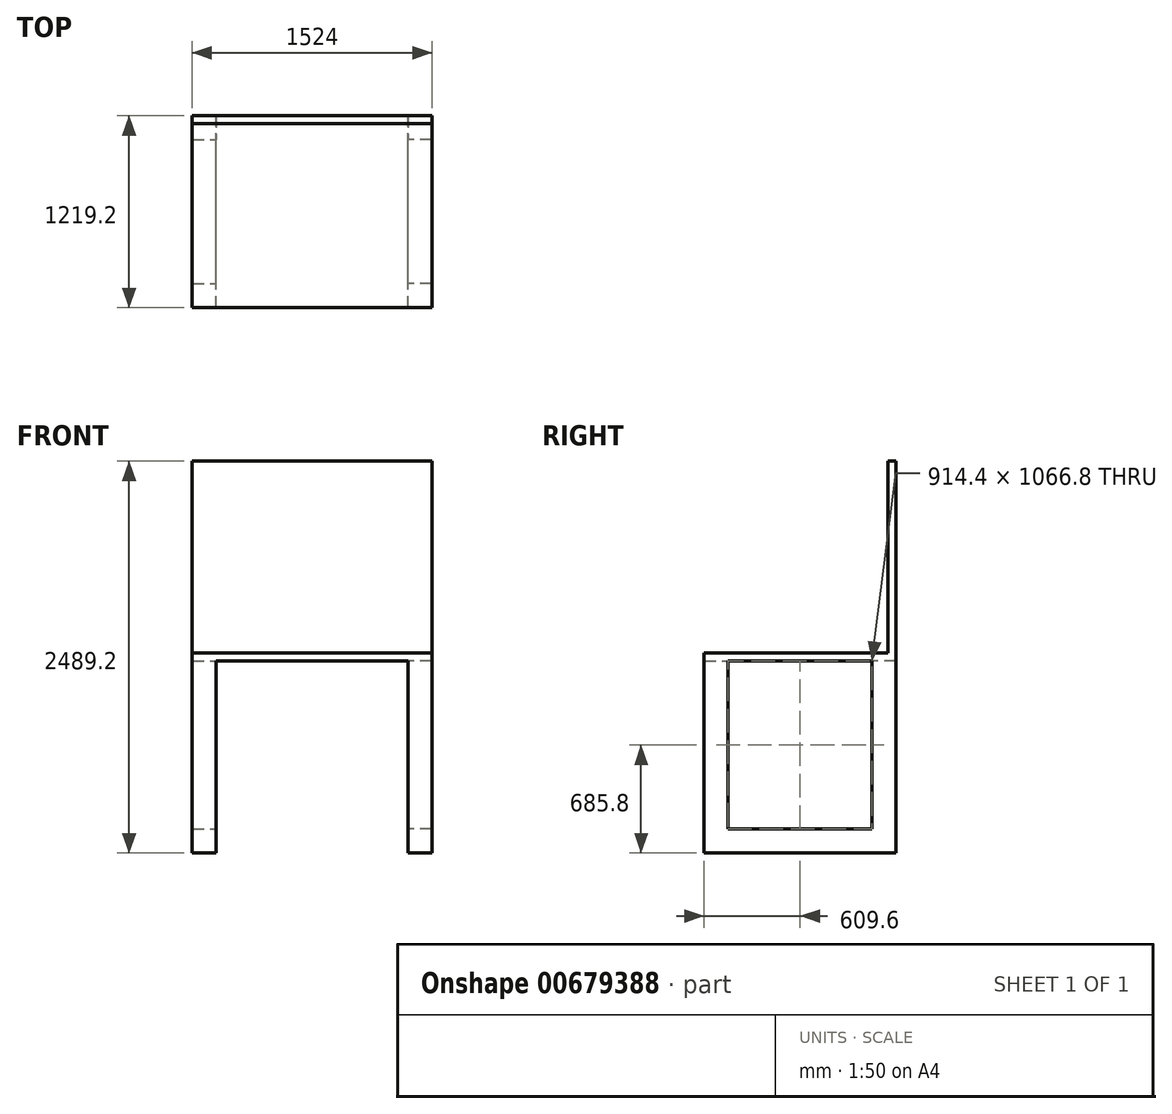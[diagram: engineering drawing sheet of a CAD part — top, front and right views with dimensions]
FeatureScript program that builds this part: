
annotation { "Feature Type Name" : "Feature", "Feature Type Description" : "" }
export const myFeature = defineFeature(function(context is Context, id is Id, definition is map)
    precondition{}
    {
        {
            var Q0;
            Q0=qCreatedBy(makeId("Front.planeOp"),FACE);
            var sketch = newSketch(context, id + "F0", { "sketchPlane" : qUnion([Q0])});
            skLineSegment(sketch, "E0.bottom", {"start": v(0, 0) * mm, "end": v(1524, 0) * mm});
            skLineSegment(sketch, "E0.top", {"start": v(0, 1219.2) * mm, "end": v(1524, 1219.2) * mm});
            skLineSegment(sketch, "E0.left", {"start": v(0, 0) * mm, "end": v(0, 1219.2) * mm});
            skLineSegment(sketch, "E0.right", {"start": v(1524, 0) * mm, "end": v(1524, 1219.2) * mm});
            skSolve(sketch);
        }
        {
            var Q0;
            Q0 = qSketchRegion(id + "F0", true);
            extrude(context, id + "F1", {"entities" : qUnion([Q0]), "depth" : 50.8 * mm, "offsetDistance" : 25.4 * mm});
        }
        {
            var Q0;
            Q0=makeQuery(id+"F1.opExtrude","SWEPT_FACE",FACE,{"disambiguationData":[OSD([sQuery(id+"F0.wireOp",EDGE,"E0.bottom")])]});
            var sketch = newSketch(context, id + "F2", { "sketchPlane" : qUnion([Q0])});
            skLineSegment(sketch, "E1.bottom", {"start": v(0, 0) * mm, "end": v(1524, 0) * mm});
            skLineSegment(sketch, "E1.top", {"start": v(0, 1219.2) * mm, "end": v(1524, 1219.2) * mm});
            skLineSegment(sketch, "E1.left", {"start": v(0, 0) * mm, "end": v(0, 1219.2) * mm});
            skLineSegment(sketch, "E1.right", {"start": v(1524, 0) * mm, "end": v(1524, 1219.2) * mm});
            skSolve(sketch);
        }
        {
            var Q0;
            Q0 = qSketchRegion(id + "F2", true);
            extrude(context, id + "F3", {"entities" : qUnion([Q0]), "operationType" : NewBodyOperationType.ADD, "depth" : 50.8 * mm, "offsetDistance" : 25.4 * mm});
        }
        {
            var Q0;
            Q0=makeQuery(id+"F3.opExtrude","CAP_FACE",FACE,{"disambiguationData":[OSD([sQuery(id+"F2.wireOp",EDGE,"E1.bottom"),sQuery(id+"F2.wireOp",EDGE,"E1.top"),sQuery(id+"F2.wireOp",EDGE,"E1.left"),sQuery(id+"F2.wireOp",EDGE,"E1.right")])],"isStart":false});
            var sketch = newSketch(context, id + "F4", { "sketchPlane" : qUnion([Q0])});
            skLineSegment(sketch, "E2.bottom", {"start": v(0, 1219.2) * mm, "end": v(152.4, 1219.2) * mm});
            skLineSegment(sketch, "E2.top", {"start": v(0, 1066.8) * mm, "end": v(152.4, 1066.8) * mm});
            skLineSegment(sketch, "E2.left", {"start": v(0, 1219.2) * mm, "end": v(0, 1066.8) * mm});
            skLineSegment(sketch, "E2.right", {"start": v(152.4, 1219.2) * mm, "end": v(152.4, 1066.8) * mm});
            skLineSegment(sketch, "E3.bottom", {"start": v(1524, 1219.2) * mm, "end": v(1371.6, 1219.2) * mm});
            skLineSegment(sketch, "E3.top", {"start": v(1524, 1066.8) * mm, "end": v(1371.6, 1066.8) * mm});
            skLineSegment(sketch, "E3.left", {"start": v(1524, 1219.2) * mm, "end": v(1524, 1066.8) * mm});
            skLineSegment(sketch, "E3.right", {"start": v(1371.6, 1219.2) * mm, "end": v(1371.6, 1066.8) * mm});
            skLineSegment(sketch, "E4.bottom", {"start": v(1524, 0) * mm, "end": v(1371.6, 0) * mm});
            skLineSegment(sketch, "E4.top", {"start": v(1524, 152.4) * mm, "end": v(1371.6, 152.4) * mm});
            skLineSegment(sketch, "E4.left", {"start": v(1524, 0) * mm, "end": v(1524, 152.4) * mm});
            skLineSegment(sketch, "E4.right", {"start": v(1371.6, 0) * mm, "end": v(1371.6, 152.4) * mm});
            skLineSegment(sketch, "E5.bottom", {"start": v(0, 0) * mm, "end": v(152.4, 0) * mm});
            skLineSegment(sketch, "E5.top", {"start": v(0, 152.4) * mm, "end": v(152.4, 152.4) * mm});
            skLineSegment(sketch, "E5.left", {"start": v(0, 0) * mm, "end": v(0, 152.4) * mm});
            skLineSegment(sketch, "E5.right", {"start": v(152.4, 0) * mm, "end": v(152.4, 152.4) * mm});
            skSolve(sketch);
        }
        {
            var Q0;
            Q0 = qSketchRegion(id + "F4", true);
            extrude(context, id + "F5", {"entities" : qUnion([Q0]), "operationType" : NewBodyOperationType.ADD, "depth" : 1219.2 * mm, "offsetDistance" : 25.4 * mm});
        }
        {
            var Q0;
            Q0=makeQuery(id+"F5.opExtrude","SWEPT_FACE",FACE,{"disambiguationData":[OSD([sQuery(id+"F4.wireOp",EDGE,"E4.top")])]});
            var sketch = newSketch(context, id + "F6", { "sketchPlane" : qUnion([Q0])});
            skLineSegment(sketch, "E6.bottom", {"start": v(1524, -1270) * mm, "end": v(1371.6, -1270) * mm});
            skLineSegment(sketch, "E6.top", {"start": v(1524, -1117.6) * mm, "end": v(1371.6, -1117.6) * mm});
            skLineSegment(sketch, "E6.left", {"start": v(1524, -1270) * mm, "end": v(1524, -1117.6) * mm});
            skLineSegment(sketch, "E6.right", {"start": v(1371.6, -1270) * mm, "end": v(1371.6, -1117.6) * mm});
            skSolve(sketch);
        }
        {
            var Q0;
            Q0 = qSketchRegion(id + "F6", true);
            extrude(context, id + "F7", {"entities" : qUnion([Q0]), "operationType" : NewBodyOperationType.ADD, "endBound" : BoundingType.UP_TO_NEXT, "depth" : 1219.2 * mm, "offsetDistance" : 25.4 * mm});
        }
        {
            var Q0;
            Q0=makeQuery(id+"F5.opExtrude","SWEPT_FACE",FACE,{"disambiguationData":[OSD([sQuery(id+"F4.wireOp",EDGE,"E5.top")])]});
            var sketch = newSketch(context, id + "F8", { "sketchPlane" : qUnion([Q0])});
            skLineSegment(sketch, "E7.bottom", {"start": v(0, -1270) * mm, "end": v(152.4, -1270) * mm});
            skLineSegment(sketch, "E7.top", {"start": v(0, -1117.6) * mm, "end": v(152.4, -1117.6) * mm});
            skLineSegment(sketch, "E7.left", {"start": v(0, -1270) * mm, "end": v(0, -1117.6) * mm});
            skLineSegment(sketch, "E7.right", {"start": v(152.4, -1270) * mm, "end": v(152.4, -1117.6) * mm});
            skSolve(sketch);
        }
        {
            var Q0;
            Q0 = qSketchRegion(id + "F8", true);
            extrude(context, id + "F9", {"entities" : qUnion([Q0]), "operationType" : NewBodyOperationType.ADD, "endBound" : BoundingType.UP_TO_NEXT, "depth" : 25.4 * mm, "offsetDistance" : 25.4 * mm});
        }
    });
